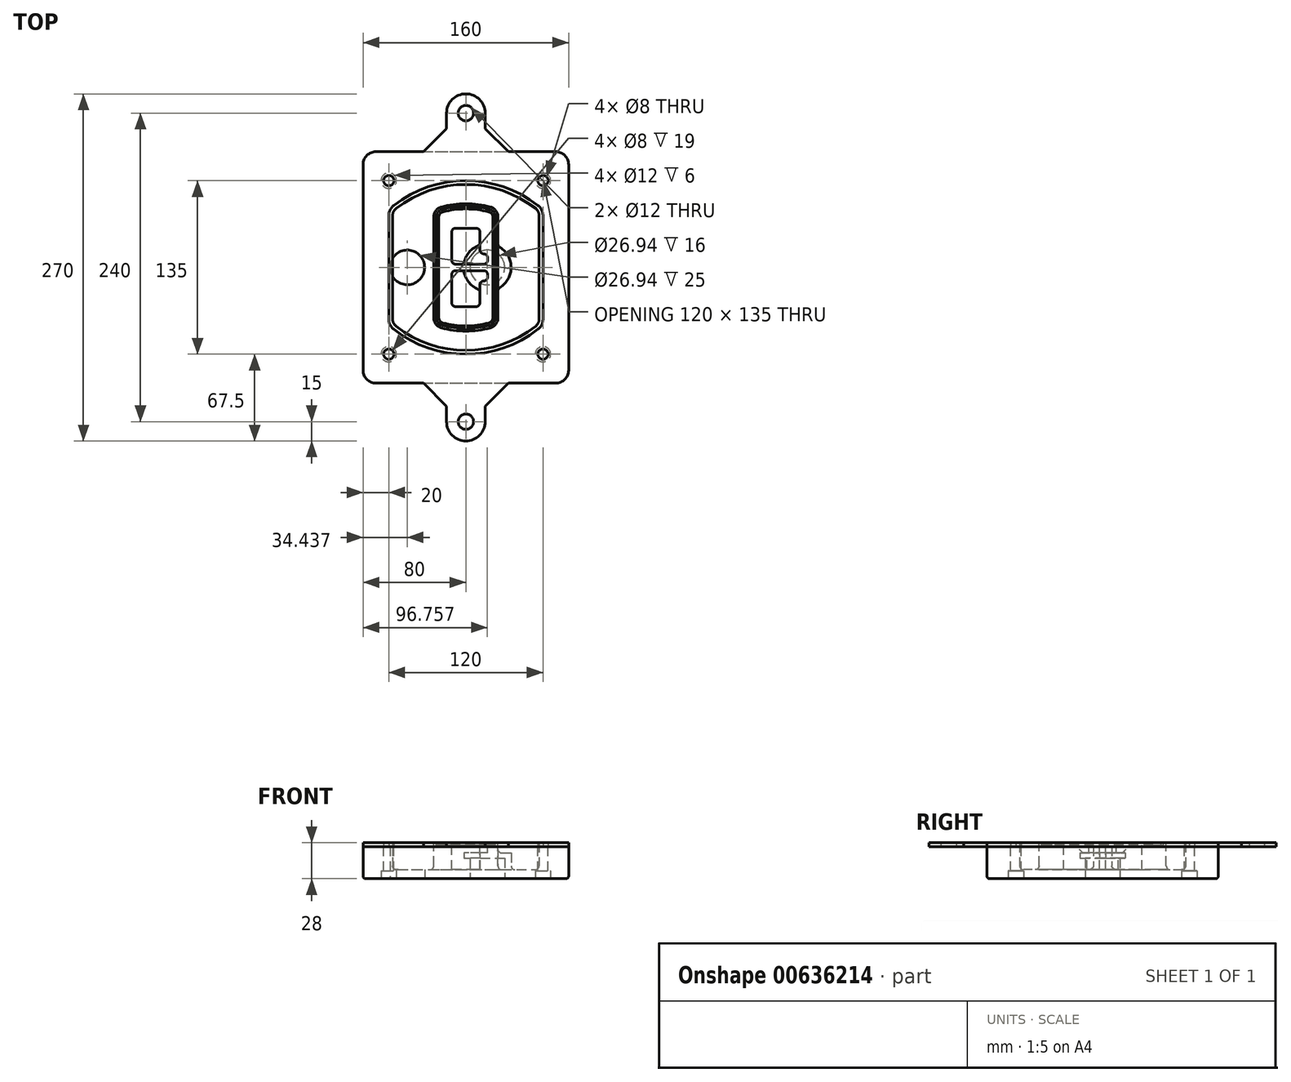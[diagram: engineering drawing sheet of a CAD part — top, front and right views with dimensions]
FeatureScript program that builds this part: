
annotation { "Feature Type Name" : "Feature", "Feature Type Description" : "" }
export const myFeature = defineFeature(function(context is Context, id is Id, definition is map)
    precondition{}
    {
        {
            var Q0;
            Q0=qCreatedBy(makeId("Top.planeOp"),FACE);
            var sketch = newSketch(context, id + "F0", { "sketchPlane" : qUnion([Q0])});
            skPoint(sketch, "E0.rect.middle", {"position": v(0, 0) * mm});
            skLineSegment(sketch, "E1.bottom", {"start": v(-70, -90) * mm, "end": v(70, -90) * mm});
            skLineSegment(sketch, "E1.top", {"start": v(-70, 90) * mm, "end": v(70, 90) * mm});
            skLineSegment(sketch, "E1.left", {"start": v(-80, -80) * mm, "end": v(-80, 80) * mm});
            skLineSegment(sketch, "E1.right", {"start": v(80, -80) * mm, "end": v(80, 80) * mm});
            skLineSegment(sketch, "E2", {"start": v(-80, 90) * mm, "end": v(80, -90) * mm, "construction": true});
            skLineSegment(sketch, "E3", {"start": v(80, 90) * mm, "end": v(-80, -90) * mm, "construction": true});
            skCircle(sketch, "E4", {"center": v(-60, 67.5) * mm, "radius": 4 * mm});
            skCircle(sketch, "E5", {"center": v(60, 67.5) * mm, "radius": 4 * mm});
            skCircle(sketch, "E6", {"center": v(60, -67.5) * mm, "radius": 4 * mm});
            skCircle(sketch, "E7", {"center": v(-60, -67.5) * mm, "radius": 4 * mm});
            skLineSegment(sketch, "E8", {"start": v(-60, 67.5) * mm, "end": v(60, 67.5) * mm, "construction": true});
            skLineSegment(sketch, "E9", {"start": v(60, 67.5) * mm, "end": v(60, -67.5) * mm, "construction": true});
            skLineSegment(sketch, "E10", {"start": v(60, -67.5) * mm, "end": v(-60, -67.5) * mm, "construction": true});
            skLineSegment(sketch, "E11", {"start": v(-60, -67.5) * mm, "end": v(-60, 67.5) * mm, "construction": true});
            skLineSegment(sketch, "E12", {"start": v(-60, 40.3) * mm, "end": v(-60, -40.3) * mm});
            skLineSegment(sketch, "E13", {"start": v(60, 40.3) * mm, "end": v(60, -40.3) * mm});
            skArc(sketch, "E14", {"start": v(56.15, 48.18) * mm, "mid": v(0, 67.5) * mm, "end": v(-56.15, 48.18) * mm});
            skArc(sketch, "E15", {"start": v(-56.15, -48.18) * mm, "mid": v(0, -67.5) * mm, "end": v(56.15, -48.18) * mm});
            skLineSegment(sketch, "E16", {"start": v(-60, 0) * mm, "end": v(60, 0) * mm, "construction": true});
            skPoint(sketch, "E17.visualSharp", {"position": v(-60, -45) * mm});
            skArc(sketch, "E17.filletArc", {"start": v(-60, -40.3) * mm, "mid": v(-58.99, -44.68) * mm, "end": v(-56.15, -48.18) * mm});
            skPoint(sketch, "E18.visualSharp", {"position": v(-60, 45) * mm});
            skArc(sketch, "E18.filletArc", {"start": v(-56.15, 48.18) * mm, "mid": v(-58.99, 44.68) * mm, "end": v(-60, 40.3) * mm});
            skPoint(sketch, "E19.visualSharp", {"position": v(60, 45) * mm});
            skArc(sketch, "E19.filletArc", {"start": v(60, 40.3) * mm, "mid": v(58.99, 44.68) * mm, "end": v(56.15, 48.18) * mm});
            skPoint(sketch, "E20.visualSharp", {"position": v(60, -45) * mm});
            skArc(sketch, "E20.filletArc", {"start": v(56.15, -48.18) * mm, "mid": v(58.99, -44.68) * mm, "end": v(60, -40.3) * mm});
            skPoint(sketch, "E21.visualSharp", {"position": v(-80, 90) * mm});
            skArc(sketch, "E21.filletArc", {"start": v(-70, 90) * mm, "mid": v(-77.07, 87.07) * mm, "end": v(-80, 80) * mm});
            skPoint(sketch, "E22.visualSharp", {"position": v(80, 90) * mm});
            skArc(sketch, "E22.filletArc", {"start": v(80, 80) * mm, "mid": v(77.07, 87.07) * mm, "end": v(70, 90) * mm});
            skPoint(sketch, "E23.visualSharp", {"position": v(80, -90) * mm});
            skArc(sketch, "E23.filletArc", {"start": v(70, -90) * mm, "mid": v(77.07, -87.07) * mm, "end": v(80, -80) * mm});
            skPoint(sketch, "E24.visualSharp", {"position": v(-80, -90) * mm});
            skArc(sketch, "E24.filletArc", {"start": v(-80, -80) * mm, "mid": v(-77.07, -87.07) * mm, "end": v(-70, -90) * mm});
            skArc(sketch, "E25.0", {"start": v(57, 40.3) * mm, "mid": v(56.3, 43.36) * mm, "end": v(54.3, 45.81) * mm});
            skLineSegment(sketch, "E25.1", {"start": v(57, 40.3) * mm, "end": v(57, -40.3) * mm});
            skArc(sketch, "E25.2", {"start": v(54.3, -45.81) * mm, "mid": v(56.3, -43.36) * mm, "end": v(57, -40.3) * mm});
            skArc(sketch, "E25.3", {"start": v(-54.3, -45.81) * mm, "mid": v(0, -64.5) * mm, "end": v(54.3, -45.81) * mm});
            skArc(sketch, "E25.4", {"start": v(-57, -40.3) * mm, "mid": v(-56.3, -43.36) * mm, "end": v(-54.3, -45.81) * mm});
            skArc(sketch, "E25.5", {"start": v(54.3, 45.81) * mm, "mid": v(0, 64.5) * mm, "end": v(-54.3, 45.81) * mm});
            skLineSegment(sketch, "E25.6", {"start": v(-57, 40.3) * mm, "end": v(-57, -40.3) * mm});
            skArc(sketch, "E25.7", {"start": v(-54.3, 45.81) * mm, "mid": v(-56.3, 43.36) * mm, "end": v(-57, 40.3) * mm});
            skArc(sketch, "E26.0", {"start": v(-58.62, 51.33) * mm, "mid": v(-62.58, 46.43) * mm, "end": v(-64, 40.3) * mm});
            skArc(sketch, "E26.1", {"start": v(58.62, 51.33) * mm, "mid": v(0, 71.5) * mm, "end": v(-58.62, 51.33) * mm});
            skArc(sketch, "E26.2", {"start": v(64, 40.3) * mm, "mid": v(62.58, 46.43) * mm, "end": v(58.62, 51.33) * mm});
            skLineSegment(sketch, "E26.3", {"start": v(64, 40.3) * mm, "end": v(64, -40.3) * mm});
            skArc(sketch, "E26.4", {"start": v(58.62, -51.33) * mm, "mid": v(62.58, -46.43) * mm, "end": v(64, -40.3) * mm});
            skLineSegment(sketch, "E26.5", {"start": v(-64, 40.3) * mm, "end": v(-64, -40.3) * mm});
            skArc(sketch, "E26.6", {"start": v(-58.62, -51.33) * mm, "mid": v(0, -71.5) * mm, "end": v(58.62, -51.33) * mm});
            skArc(sketch, "E26.7", {"start": v(-64, -40.3) * mm, "mid": v(-62.58, -46.43) * mm, "end": v(-58.62, -51.33) * mm});
            skSolve(sketch);
        }
        {
            var Q0;
            Q0=makeQuery(id+"F0.imprint","IMPRINT",FACE,{"disambiguationData":[TD([[makeQuery(id+"F0.imprint","IMPRINT",EDGE,{"derivedFrom":sQuery(id+"F0.wireOp",EDGE,"E1.bottom")}),1.0]])]});
            var Q1;
            Q1=makeQuery(id+"F0.imprint","IMPRINT",FACE,{"disambiguationData":[TD([[makeQuery(id+"F0.imprint","IMPRINT",EDGE,{"derivedFrom":sQuery(id+"F0.wireOp",EDGE,"E12")}),1.0]])]});
            var Q2;
            Q2=makeQuery(id+"F0.imprint","IMPRINT",FACE,{"disambiguationData":[TD([[makeQuery(id+"F0.imprint","IMPRINT",EDGE,{"derivedFrom":sQuery(id+"F0.wireOp",EDGE,"E25.0")}),1.0]])]});
            var Q3;
            Q3=makeQuery(id+"F0.imprint","IMPRINT",FACE,{"disambiguationData":[TD([[makeQuery(id+"F0.imprint","IMPRINT",EDGE,{"derivedFrom":sQuery(id+"F0.wireOp",EDGE,"E12")}),-1.0]])]});
            extrude(context, id + "F1", {"entities" : qUnion([Q0, Q1, Q2, Q3]), "oppositeDirection" : true, "depth" : 25 * mm});
        }
        {
            var Q0;
            Q0=makeQuery(id+"F0.imprint","IMPRINT",FACE,{"disambiguationData":[TD([[makeQuery(id+"F0.imprint","IMPRINT",EDGE,{"derivedFrom":sQuery(id+"F0.wireOp",EDGE,"E12")}),1.0]])]});
            extrude(context, id + "F2", {"entities" : qUnion([Q0]), "operationType" : NewBodyOperationType.ADD, "depth" : 3 * mm});
        }
        {
            var Q0;
            Q0=makeQuery(id+"F0.imprint","IMPRINT",FACE,{"disambiguationData":[TD([[makeQuery(id+"F0.imprint","IMPRINT",EDGE,{"derivedFrom":sQuery(id+"F0.wireOp",EDGE,"E25.0")}),1.0]])]});
            extrude(context, id + "F3", {"entities" : qUnion([Q0]), "operationType" : NewBodyOperationType.REMOVE, "oppositeDirection" : true, "depth" : 18 * mm});
        }
        {
            var Q0;
            Q0=makeQuery(id+"F2.opExtrude","CAP_FACE",FACE,{"disambiguationData":[OSD([sQuery(id+"F0.wireOp",EDGE,"E12"),sQuery(id+"F0.wireOp",EDGE,"E13"),sQuery(id+"F0.wireOp",EDGE,"E14"),sQuery(id+"F0.wireOp",EDGE,"E15"),sQuery(id+"F0.wireOp",EDGE,"E17.filletArc"),sQuery(id+"F0.wireOp",EDGE,"E18.filletArc"),sQuery(id+"F0.wireOp",EDGE,"E19.filletArc"),sQuery(id+"F0.wireOp",EDGE,"E20.filletArc"),sQuery(id+"F0.wireOp",EDGE,"E25.0"),sQuery(id+"F0.wireOp",EDGE,"E25.1"),sQuery(id+"F0.wireOp",EDGE,"E25.2"),sQuery(id+"F0.wireOp",EDGE,"E25.3"),sQuery(id+"F0.wireOp",EDGE,"E25.4"),sQuery(id+"F0.wireOp",EDGE,"E25.5"),sQuery(id+"F0.wireOp",EDGE,"E25.6"),sQuery(id+"F0.wireOp",EDGE,"E25.7")])],"isStart":false});
            var sketch = newSketch(context, id + "F4", { "sketchPlane" : qUnion([Q0])});
            skArc(sketch, "E27.0", {"start": v(-19.08, -46.97) * mm, "mid": v(0, -49.5) * mm, "end": v(19.08, -46.97) * mm});
            skArc(sketch, "E28.0", {"start": v(19.08, 46.97) * mm, "mid": v(0, 49.5) * mm, "end": v(-19.08, 46.97) * mm});
            skLineSegment(sketch, "E29", {"start": v(-25, 39.25) * mm, "end": v(-25, -39.25) * mm});
            skLineSegment(sketch, "E30", {"start": v(25, 39.25) * mm, "end": v(25, -39.25) * mm});
            skLineSegment(sketch, "E31", {"start": v(-25, 45.1) * mm, "end": v(25, 45.1) * mm, "construction": true});
            skLineSegment(sketch, "E32", {"start": v(-25, -45.1) * mm, "end": v(25, -45.1) * mm, "construction": true});
            skPoint(sketch, "E33.visualSharp", {"position": v(-25, 45.1) * mm});
            skArc(sketch, "E33.filletArc", {"start": v(-19.08, 46.97) * mm, "mid": v(-23.35, 44.11) * mm, "end": v(-25, 39.25) * mm});
            skPoint(sketch, "E34.visualSharp", {"position": v(25, 45.1) * mm});
            skArc(sketch, "E34.filletArc", {"start": v(25, 39.25) * mm, "mid": v(23.35, 44.11) * mm, "end": v(19.08, 46.97) * mm});
            skPoint(sketch, "E35.visualSharp", {"position": v(25, -45.1) * mm});
            skArc(sketch, "E35.filletArc", {"start": v(19.08, -46.97) * mm, "mid": v(23.35, -44.11) * mm, "end": v(25, -39.25) * mm});
            skPoint(sketch, "E36.visualSharp", {"position": v(-25, -45.1) * mm});
            skArc(sketch, "E36.filletArc", {"start": v(-25, -39.25) * mm, "mid": v(-23.35, -44.11) * mm, "end": v(-19.08, -46.97) * mm});
            skArc(sketch, "E37.0", {"start": v(54.3, 45.81) * mm, "mid": v(0, 64.5) * mm, "end": v(-54.3, 45.81) * mm});
            skArc(sketch, "E37.1", {"start": v(-54.3, 45.81) * mm, "mid": v(-56.3, 43.36) * mm, "end": v(-57, 40.3) * mm});
            skLineSegment(sketch, "E37.2", {"start": v(-57, 40.3) * mm, "end": v(-57, -40.3) * mm});
            skArc(sketch, "E37.3", {"start": v(-57, -40.3) * mm, "mid": v(-56.3, -43.36) * mm, "end": v(-54.3, -45.81) * mm});
            skArc(sketch, "E37.4", {"start": v(-54.3, -45.81) * mm, "mid": v(0, -64.5) * mm, "end": v(54.3, -45.81) * mm});
            skArc(sketch, "E37.5", {"start": v(54.3, -45.81) * mm, "mid": v(56.3, -43.36) * mm, "end": v(57, -40.3) * mm});
            skLineSegment(sketch, "E37.6", {"start": v(57, 40.3) * mm, "end": v(57, -40.3) * mm});
            skArc(sketch, "E37.7", {"start": v(57, 40.3) * mm, "mid": v(56.3, 43.36) * mm, "end": v(54.3, 45.81) * mm});
            skLineSegment(sketch, "E38.0", {"start": v(23, 39.25) * mm, "end": v(23, -39.25) * mm});
            skArc(sketch, "E38.1", {"start": v(18.56, -45.04) * mm, "mid": v(21.76, -42.9) * mm, "end": v(23, -39.25) * mm});
            skArc(sketch, "E38.2", {"start": v(-18.56, -45.04) * mm, "mid": v(0, -47.5) * mm, "end": v(18.56, -45.04) * mm});
            skArc(sketch, "E38.3", {"start": v(-23, -39.25) * mm, "mid": v(-21.76, -42.9) * mm, "end": v(-18.56, -45.04) * mm});
            skLineSegment(sketch, "E38.4", {"start": v(-23, 39.25) * mm, "end": v(-23, -39.25) * mm});
            skArc(sketch, "E38.5", {"start": v(23, 39.25) * mm, "mid": v(21.76, 42.9) * mm, "end": v(18.56, 45.04) * mm});
            skArc(sketch, "E38.6", {"start": v(-18.56, 45.04) * mm, "mid": v(-21.76, 42.9) * mm, "end": v(-23, 39.25) * mm});
            skArc(sketch, "E38.7", {"start": v(18.56, 45.04) * mm, "mid": v(0, 47.5) * mm, "end": v(-18.56, 45.04) * mm});
            skArc(sketch, "E39.0", {"start": v(21, 39.25) * mm, "mid": v(20.18, 41.68) * mm, "end": v(18.04, 43.1) * mm});
            skLineSegment(sketch, "E39.1", {"start": v(21, 39.25) * mm, "end": v(21, -39.25) * mm});
            skArc(sketch, "E39.2", {"start": v(18.04, -43.1) * mm, "mid": v(20.18, -41.68) * mm, "end": v(21, -39.25) * mm});
            skArc(sketch, "E39.3", {"start": v(-18.04, -43.1) * mm, "mid": v(0, -45.5) * mm, "end": v(18.04, -43.1) * mm});
            skArc(sketch, "E39.4", {"start": v(-21, -39.25) * mm, "mid": v(-20.18, -41.68) * mm, "end": v(-18.04, -43.1) * mm});
            skArc(sketch, "E39.5", {"start": v(18.04, 43.1) * mm, "mid": v(0, 45.5) * mm, "end": v(-18.04, 43.1) * mm});
            skLineSegment(sketch, "E39.6", {"start": v(-21, 39.25) * mm, "end": v(-21, -39.25) * mm});
            skArc(sketch, "E39.7", {"start": v(-18.04, 43.1) * mm, "mid": v(-20.18, 41.68) * mm, "end": v(-21, 39.25) * mm});
            skLineSegment(sketch, "E40", {"start": v(-25, 0) * mm, "end": v(25, 0) * mm, "construction": true});
            skLineSegment(sketch, "E41", {"start": v(-11, 5.5) * mm, "end": v(-11, 27.5) * mm});
            skLineSegment(sketch, "E42", {"start": v(-8, 30.5) * mm, "end": v(8, 30.5) * mm});
            skLineSegment(sketch, "E43", {"start": v(11, 27.5) * mm, "end": v(11, 13.5) * mm});
            skLineSegment(sketch, "E44", {"start": v(14, 10.5) * mm, "end": v(14, 10.5) * mm});
            skLineSegment(sketch, "E45", {"start": v(17, 7.5) * mm, "end": v(17, 5.5) * mm});
            skLineSegment(sketch, "E46", {"start": v(14, 2.5) * mm, "end": v(-8, 2.5) * mm});
            skPoint(sketch, "E47.visualSharp", {"position": v(-11, 30.5) * mm});
            skArc(sketch, "E47.filletArc", {"start": v(-8, 30.5) * mm, "mid": v(-10.12, 29.62) * mm, "end": v(-11, 27.5) * mm});
            skPoint(sketch, "E48.visualSharp", {"position": v(11, 30.5) * mm});
            skArc(sketch, "E48.filletArc", {"start": v(11, 27.5) * mm, "mid": v(10.12, 29.62) * mm, "end": v(8, 30.5) * mm});
            skPoint(sketch, "E49.visualSharp", {"position": v(11, 10.5) * mm});
            skArc(sketch, "E49.filletArc", {"start": v(11, 13.5) * mm, "mid": v(11.88, 11.38) * mm, "end": v(14, 10.5) * mm});
            skPoint(sketch, "E50.visualSharp", {"position": v(17, 10.5) * mm});
            skArc(sketch, "E50.filletArc", {"start": v(17, 7.5) * mm, "mid": v(16.12, 9.62) * mm, "end": v(14, 10.5) * mm});
            skPoint(sketch, "E51.visualSharp", {"position": v(17, 2.5) * mm});
            skArc(sketch, "E51.filletArc", {"start": v(14, 2.5) * mm, "mid": v(16.12, 3.38) * mm, "end": v(17, 5.5) * mm});
            skPoint(sketch, "E52.visualSharp", {"position": v(-11, 2.5) * mm});
            skArc(sketch, "E52.filletArc", {"start": v(-11, 5.5) * mm, "mid": v(-10.12, 3.38) * mm, "end": v(-8, 2.5) * mm});
            skLineSegment(sketch, "E53.0.MirrorCS", {"start": v(14, -2.5) * mm, "end": v(-8, -2.5) * mm});
            skArc(sketch, "E54.0.MirrorCS", {"start": v(-11, -5.5) * mm, "mid": v(-10.12, -3.38) * mm, "end": v(-8, -2.5) * mm});
            skLineSegment(sketch, "E55.0.MirrorCS", {"start": v(-11, -5.5) * mm, "end": v(-11, -27.5) * mm});
            skArc(sketch, "E56.0.MirrorCS", {"start": v(-8, -30.5) * mm, "mid": v(-10.12, -29.62) * mm, "end": v(-11, -27.5) * mm});
            skLineSegment(sketch, "E57.0.MirrorCS", {"start": v(-8, -30.5) * mm, "end": v(8, -30.5) * mm});
            skArc(sketch, "E58.0.MirrorCS", {"start": v(11, -27.5) * mm, "mid": v(10.12, -29.62) * mm, "end": v(8, -30.5) * mm});
            skLineSegment(sketch, "E59.0.MirrorCS", {"start": v(11, -27.5) * mm, "end": v(11, -13.5) * mm});
            skArc(sketch, "E60.0.MirrorCS", {"start": v(11, -13.5) * mm, "mid": v(11.88, -11.38) * mm, "end": v(14, -10.5) * mm});
            skArc(sketch, "E61.0.MirrorCS", {"start": v(17, -7.5) * mm, "mid": v(16.12, -9.62) * mm, "end": v(14, -10.5) * mm});
            skLineSegment(sketch, "E62.0.MirrorCS", {"start": v(17, -7.5) * mm, "end": v(17, -5.5) * mm});
            skArc(sketch, "E63.0.MirrorCS", {"start": v(14, -2.5) * mm, "mid": v(16.12, -3.38) * mm, "end": v(17, -5.5) * mm});
            skSolve(sketch);
        }
        {
            var Q0;
            Q0=makeQuery(id+"F4.imprint","IMPRINT",FACE,{"disambiguationData":[TD([[makeQuery(id+"F4.imprint","IMPRINT",EDGE,{"derivedFrom":sQuery(id+"F4.wireOp",EDGE,"E27.0")}),1.0]])]});
            var Q1;
            Q1=makeQuery(id+"F4.imprint","IMPRINT",FACE,{"disambiguationData":[TD([[makeQuery(id+"F4.imprint","IMPRINT",EDGE,{"derivedFrom":sQuery(id+"F4.wireOp",EDGE,"E38.0")}),-1.0]])]});
            var Q2;
            Q2=makeQuery(id+"F4.imprint","IMPRINT",FACE,{"disambiguationData":[TD([[makeQuery(id+"F4.imprint","IMPRINT",EDGE,{"derivedFrom":sQuery(id+"F4.wireOp",EDGE,"E39.0")}),1.0]])]});
            extrude(context, id + "F5", {"entities" : qUnion([Q0, Q1, Q2]), "operationType" : NewBodyOperationType.ADD, "endBound" : BoundingType.UP_TO_NEXT, "oppositeDirection" : true, "depth" : 25 * mm});
        }
        {
            var Q0;
            Q0=makeQuery(id+"F4.imprint","IMPRINT",FACE,{"disambiguationData":[TD([[makeQuery(id+"F4.imprint","IMPRINT",EDGE,{"derivedFrom":sQuery(id+"F4.wireOp",EDGE,"E38.0")}),-1.0]])]});
            extrude(context, id + "F6", {"entities" : qUnion([Q0]), "operationType" : NewBodyOperationType.REMOVE, "oppositeDirection" : true, "depth" : 2 * mm});
        }
        {
            var Q0;
            Q0=makeQuery(id+"F1.opExtrude","CAP_FACE",FACE,{"disambiguationData":[OSD([sQuery(id+"F0.wireOp",EDGE,"E1.bottom"),sQuery(id+"F0.wireOp",EDGE,"E1.top"),sQuery(id+"F0.wireOp",EDGE,"E1.left"),sQuery(id+"F0.wireOp",EDGE,"E1.right"),sQuery(id+"F0.wireOp",EDGE,"E4"),sQuery(id+"F0.wireOp",EDGE,"E5"),sQuery(id+"F0.wireOp",EDGE,"E6"),sQuery(id+"F0.wireOp",EDGE,"E7"),sQuery(id+"F0.wireOp",EDGE,"E21.filletArc"),sQuery(id+"F0.wireOp",EDGE,"E22.filletArc"),sQuery(id+"F0.wireOp",EDGE,"E23.filletArc"),sQuery(id+"F0.wireOp",EDGE,"E24.filletArc")])],"isStart":false});
            var sketch = newSketch(context, id + "F7", { "sketchPlane" : qUnion([Q0])});
            skCircle(sketch, "E64", {"center": v(16.76, 0) * mm, "radius": 13.47 * mm});
            skCircle(sketch, "E65", {"center": v(-45.56, 0) * mm, "radius": 13.47 * mm});
            skLineSegment(sketch, "E66", {"start": v(80, 0) * mm, "end": v(-80, 0) * mm});
            skCircle(sketch, "E67", {"center": v(16.76, 0) * mm, "radius": 18.47 * mm});
            skCircle(sketch, "E68", {"center": v(60, -67.5) * mm, "radius": 6 * mm});
            skCircle(sketch, "E69", {"center": v(-60, -67.5) * mm, "radius": 6 * mm});
            skCircle(sketch, "E70", {"center": v(-60, 67.5) * mm, "radius": 6 * mm});
            skCircle(sketch, "E71", {"center": v(60, 67.5) * mm, "radius": 6 * mm});
            skSolve(sketch);
        }
        {
            var Q0;
            {var subQ1=sQuery(id+"F7.wireOp",EDGE,"E66");var subQ4=sQuery(id+"F7.wireOp",EDGE,"E64");var subQ6=makeQuery(id+"F7.imprint","INTERSECT",VERTEX,{"disambiguationData":[OD(0.0)],"derivedFrom":[subQ4,subQ1]});Q0=makeQuery(id+"F7.imprint","IMPRINT",FACE,{"disambiguationData":[TD([[makeQuery(id+"F7.imprint","IMPRINT",EDGE,{"disambiguationData":[TD([[subQ6,-1.0]])],"derivedFrom":subQ4}),-1.0]])]});}
            var Q1;
            {var subQ0=sQuery(id+"F7.wireOp",EDGE,"E66");var subQ1=sQuery(id+"F7.wireOp",EDGE,"E64");var subQ3=makeQuery(id+"F7.imprint","INTERSECT",VERTEX,{"disambiguationData":[OD(0.0)],"derivedFrom":[subQ1,subQ0]});Q1=makeQuery(id+"F7.imprint","IMPRINT",FACE,{"disambiguationData":[TD([[makeQuery(id+"F7.imprint","IMPRINT",EDGE,{"disambiguationData":[TD([[subQ3,-1.0]])],"derivedFrom":subQ1}),1.0]])]});}
            var Q2;
            {var subQ0=sQuery(id+"F7.wireOp",EDGE,"E66");var subQ1=sQuery(id+"F7.wireOp",EDGE,"E64");var subQ3=makeQuery(id+"F7.imprint","INTERSECT",VERTEX,{"disambiguationData":[OD(0.0)],"derivedFrom":[subQ1,subQ0]});Q2=makeQuery(id+"F7.imprint","IMPRINT",FACE,{"disambiguationData":[TD([[makeQuery(id+"F7.imprint","IMPRINT",EDGE,{"disambiguationData":[TD([[subQ3,1.0]])],"derivedFrom":subQ1}),1.0]])]});}
            var Q3;
            {var subQ1=sQuery(id+"F7.wireOp",EDGE,"E66");var subQ4=sQuery(id+"F7.wireOp",EDGE,"E64");var subQ6=makeQuery(id+"F7.imprint","INTERSECT",VERTEX,{"disambiguationData":[OD(0.0)],"derivedFrom":[subQ4,subQ1]});Q3=makeQuery(id+"F7.imprint","IMPRINT",FACE,{"disambiguationData":[TD([[makeQuery(id+"F7.imprint","IMPRINT",EDGE,{"disambiguationData":[TD([[subQ6,1.0]])],"derivedFrom":subQ4}),-1.0]])]});}
            extrude(context, id + "F8", {"entities" : qUnion([Q0, Q1, Q2, Q3]), "operationType" : NewBodyOperationType.ADD, "oppositeDirection" : true, "depth" : 20 * mm});
        }
        {
            var Q0;
            {var subQ0=sQuery(id+"F7.wireOp",EDGE,"E66");var subQ1=sQuery(id+"F7.wireOp",EDGE,"E64");var subQ3=makeQuery(id+"F7.imprint","INTERSECT",VERTEX,{"disambiguationData":[OD(0.0)],"derivedFrom":[subQ1,subQ0]});Q0=makeQuery(id+"F7.imprint","IMPRINT",FACE,{"disambiguationData":[TD([[makeQuery(id+"F7.imprint","IMPRINT",EDGE,{"disambiguationData":[TD([[subQ3,-1.0]])],"derivedFrom":subQ1}),1.0]])]});}
            var Q1;
            {var subQ0=sQuery(id+"F7.wireOp",EDGE,"E66");var subQ1=sQuery(id+"F7.wireOp",EDGE,"E64");var subQ3=makeQuery(id+"F7.imprint","INTERSECT",VERTEX,{"disambiguationData":[OD(0.0)],"derivedFrom":[subQ1,subQ0]});Q1=makeQuery(id+"F7.imprint","IMPRINT",FACE,{"disambiguationData":[TD([[makeQuery(id+"F7.imprint","IMPRINT",EDGE,{"disambiguationData":[TD([[subQ3,1.0]])],"derivedFrom":subQ1}),1.0]])]});}
            extrude(context, id + "F9", {"entities" : qUnion([Q0, Q1]), "operationType" : NewBodyOperationType.REMOVE, "oppositeDirection" : true, "depth" : 16 * mm});
        }
        {
            var Q0;
            {var subQ0=sQuery(id+"F7.wireOp",EDGE,"E66");var subQ1=sQuery(id+"F7.wireOp",EDGE,"E65");var subQ3=makeQuery(id+"F7.imprint","INTERSECT",VERTEX,{"disambiguationData":[OD(0.0)],"derivedFrom":[subQ1,subQ0]});Q0=makeQuery(id+"F7.imprint","IMPRINT",FACE,{"disambiguationData":[TD([[makeQuery(id+"F7.imprint","IMPRINT",EDGE,{"disambiguationData":[TD([[subQ3,-1.0]])],"derivedFrom":subQ1}),1.0]])]});}
            var Q1;
            {var subQ0=sQuery(id+"F7.wireOp",EDGE,"E66");var subQ1=sQuery(id+"F7.wireOp",EDGE,"E65");var subQ3=makeQuery(id+"F7.imprint","INTERSECT",VERTEX,{"disambiguationData":[OD(0.0)],"derivedFrom":[subQ1,subQ0]});Q1=makeQuery(id+"F7.imprint","IMPRINT",FACE,{"disambiguationData":[TD([[makeQuery(id+"F7.imprint","IMPRINT",EDGE,{"disambiguationData":[TD([[subQ3,1.0]])],"derivedFrom":subQ1}),1.0]])]});}
            extrude(context, id + "F10", {"entities" : qUnion([Q0, Q1]), "operationType" : NewBodyOperationType.REMOVE, "oppositeDirection" : true, "depth" : 25 * mm});
        }
        {
            var Q0;
            Q0=makeQuery(id+"F7.imprint","IMPRINT",FACE,{"disambiguationData":[TD([[makeQuery(id+"F7.imprint","IMPRINT",EDGE,{"derivedFrom":sQuery(id+"F7.wireOp",EDGE,"E68")}),1.0]])]});
            var Q1;
            Q1=makeQuery(id+"F7.imprint","IMPRINT",FACE,{"disambiguationData":[TD([[makeQuery(id+"F7.imprint","IMPRINT",EDGE,{"derivedFrom":makeQuery(id+"F1.opExtrude","CAP_EDGE",EDGE,{"disambiguationData":[OSD([sQuery(id+"F0.wireOp",EDGE,"E5")])],"isStart":false})}),-1.0]])]});
            var Q2;
            Q2=makeQuery(id+"F7.imprint","IMPRINT",FACE,{"disambiguationData":[TD([[makeQuery(id+"F7.imprint","IMPRINT",EDGE,{"derivedFrom":sQuery(id+"F7.wireOp",EDGE,"E69")}),1.0]])]});
            var Q3;
            Q3=makeQuery(id+"F7.imprint","IMPRINT",FACE,{"disambiguationData":[TD([[makeQuery(id+"F7.imprint","IMPRINT",EDGE,{"derivedFrom":makeQuery(id+"F1.opExtrude","CAP_EDGE",EDGE,{"disambiguationData":[OSD([sQuery(id+"F0.wireOp",EDGE,"E4")])],"isStart":false})}),-1.0]])]});
            var Q4;
            Q4=makeQuery(id+"F7.imprint","IMPRINT",FACE,{"disambiguationData":[TD([[makeQuery(id+"F7.imprint","IMPRINT",EDGE,{"derivedFrom":sQuery(id+"F7.wireOp",EDGE,"E70")}),1.0]])]});
            var Q5;
            Q5=makeQuery(id+"F7.imprint","IMPRINT",FACE,{"disambiguationData":[TD([[makeQuery(id+"F7.imprint","IMPRINT",EDGE,{"derivedFrom":makeQuery(id+"F1.opExtrude","CAP_EDGE",EDGE,{"disambiguationData":[OSD([sQuery(id+"F0.wireOp",EDGE,"E7")])],"isStart":false})}),-1.0]])]});
            var Q6;
            Q6=makeQuery(id+"F7.imprint","IMPRINT",FACE,{"disambiguationData":[TD([[makeQuery(id+"F7.imprint","IMPRINT",EDGE,{"derivedFrom":sQuery(id+"F7.wireOp",EDGE,"E71")}),1.0]])]});
            var Q7;
            Q7=makeQuery(id+"F7.imprint","IMPRINT",FACE,{"disambiguationData":[TD([[makeQuery(id+"F7.imprint","IMPRINT",EDGE,{"derivedFrom":makeQuery(id+"F1.opExtrude","CAP_EDGE",EDGE,{"disambiguationData":[OSD([sQuery(id+"F0.wireOp",EDGE,"E6")])],"isStart":false})}),-1.0]])]});
            extrude(context, id + "F11", {"entities" : qUnion([Q0, Q1, Q2, Q3, Q4, Q5, Q6, Q7]), "operationType" : NewBodyOperationType.REMOVE, "oppositeDirection" : true, "depth" : 6 * mm});
        }
        {
            var Q0;
            Q0=makeQuery(id+"F9.boolean.opBoolean","COPY",FACE,{"derivedFrom":makeQuery(id+"F9.opExtrude","CAP_FACE",FACE,{"disambiguationData":[OSD([sQuery(id+"F7.wireOp",EDGE,"E64")])],"isStart":false})});
            var sketch = newSketch(context, id + "F12", { "sketchPlane" : qUnion([Q0])});
            skArc(sketch, "E72.0", {"start": v(11, 17.55) * mm, "mid": v(2.57, 11.82) * mm, "end": v(-1.54, 2.5) * mm});
            skArc(sketch, "E72.1", {"start": v(-1.54, -2.5) * mm, "mid": v(2.57, -11.82) * mm, "end": v(11, -17.55) * mm});
            skLineSegment(sketch, "E73", {"start": v(-1.54, -2.5) * mm, "end": v(14, -2.5) * mm});
            skLineSegment(sketch, "E74.0", {"start": v(14, 2.5) * mm, "end": v(-1.54, 2.5) * mm});
            skArc(sketch, "E74.1", {"start": v(14, 2.5) * mm, "mid": v(16.12, 3.38) * mm, "end": v(17, 5.5) * mm});
            skLineSegment(sketch, "E74.2", {"start": v(17, 7.5) * mm, "end": v(17, 5.5) * mm});
            skArc(sketch, "E74.3", {"start": v(17, 7.5) * mm, "mid": v(16.12, 9.62) * mm, "end": v(14, 10.5) * mm});
            skArc(sketch, "E74.4", {"start": v(11, 13.5) * mm, "mid": v(11.88, 11.38) * mm, "end": v(14, 10.5) * mm});
            skLineSegment(sketch, "E74.5", {"start": v(11, 17.55) * mm, "end": v(11, 13.5) * mm});
            skLineSegment(sketch, "E74.7", {"start": v(14, -2.5) * mm, "end": v(-1.54, -2.5) * mm});
            skArc(sketch, "E74.8", {"start": v(14, -2.5) * mm, "mid": v(16.12, -3.38) * mm, "end": v(17, -5.5) * mm});
            skLineSegment(sketch, "E74.9", {"start": v(17, -7.5) * mm, "end": v(17, -5.5) * mm});
            skArc(sketch, "E74.10", {"start": v(17, -7.5) * mm, "mid": v(16.12, -9.62) * mm, "end": v(14, -10.5) * mm});
            skArc(sketch, "E74.11", {"start": v(11, -13.5) * mm, "mid": v(11.88, -11.38) * mm, "end": v(14, -10.5) * mm});
            skLineSegment(sketch, "E74.12", {"start": v(11, -17.55) * mm, "end": v(11, -13.5) * mm});
            skPoint(sketch, "E75.orphan", {"position": v(11, -27.5) * mm});
            skPoint(sketch, "E76.orphan", {"position": v(-8, -2.5) * mm});
            skPoint(sketch, "E77.orphan", {"position": v(-8, 2.5) * mm});
            skPoint(sketch, "E78.orphan", {"position": v(11, 27.5) * mm});
            skSolve(sketch);
        }
        {
            var Q0;
            {var subQ7=sQuery(id+"F12.wireOp",EDGE,"E72.0");var subQ14=sQuery(id+"F12.wireOp",EDGE,"E72.1");var subQ16=sQuery(id+"F12.wireOp",EDGE,"E74.1");var subQ18=sQuery(id+"F12.wireOp",EDGE,"E74.8");Q0=qUnion([makeQuery(id+"F12.imprint","IMPRINT",FACE,{"disambiguationData":[TD([[makeQuery(id+"F12.imprint","IMPRINT",EDGE,{"derivedFrom":subQ7}),1.0]])]}),makeQuery(id+"F12.imprint","IMPRINT",FACE,{"disambiguationData":[TD([[makeQuery(id+"F12.imprint","IMPRINT",EDGE,{"derivedFrom":subQ14}),1.0]])]}),makeQuery(id+"F12.imprint","IMPRINT",FACE,{"disambiguationData":[TD([[makeQuery(id+"F12.imprint","IMPRINT",EDGE,{"derivedFrom":subQ16}),1.0]])]}),makeQuery(id+"F12.imprint","IMPRINT",FACE,{"disambiguationData":[TD([[makeQuery(id+"F12.imprint","IMPRINT",EDGE,{"derivedFrom":subQ18}),-1.0]])]})]);}
            var Q1;
            Q1=makeQuery(id+"F5.boolean.opBoolean","SPLIT",FACE,{"disambiguationData":[TD([makeQuery(id+"F5.opExtrude","SWEPT_FACE",FACE,{"disambiguationData":[OSD([sQuery(id+"F4.wireOp",EDGE,"E41")])]})])],"derivedFrom":makeQuery(id+"F3.boolean.opBoolean","COPY",FACE,{"derivedFrom":makeQuery(id+"F3.opExtrude","CAP_FACE",FACE,{"disambiguationData":[OSD([sQuery(id+"F0.wireOp",EDGE,"E25.0"),sQuery(id+"F0.wireOp",EDGE,"E25.1"),sQuery(id+"F0.wireOp",EDGE,"E25.2"),sQuery(id+"F0.wireOp",EDGE,"E25.3"),sQuery(id+"F0.wireOp",EDGE,"E25.4"),sQuery(id+"F0.wireOp",EDGE,"E25.5"),sQuery(id+"F0.wireOp",EDGE,"E25.6"),sQuery(id+"F0.wireOp",EDGE,"E25.7")])],"isStart":false})})});
            extrude(context, id + "F13", {"entities" : qUnion([Q0]), "operationType" : NewBodyOperationType.REMOVE, "endBound" : BoundingType.UP_TO_SURFACE, "endBoundEntityFace" : qUnion([Q1]), "depth" : 25 * mm});
        }
        {
            var Q0;
            Q0=makeQuery(id+"F3.boolean.opBoolean","COPY",EDGE,{"derivedFrom":makeQuery(id+"F3.opExtrude","CAP_EDGE",EDGE,{"disambiguationData":[OSD([sQuery(id+"F0.wireOp",EDGE,"E25.6")])],"isStart":false})});
            var Q1;
            Q1=makeQuery(id+"F8.boolean.opBoolean","INTERSECT",EDGE,{"derivedFrom":[makeQuery(id+"F5.opExtrude","SWEPT_FACE",FACE,{"disambiguationData":[OSD([sQuery(id+"F4.wireOp",EDGE,"E30")])]}),makeQuery(id+"F8.opExtrude","CAP_FACE",FACE,{"disambiguationData":[OSD([sQuery(id+"F7.wireOp",EDGE,"E67")])],"isStart":false})]});
            var Q2;
            Q2=makeQuery(id+"F8.boolean.opBoolean","INTERSECT",EDGE,{"disambiguationData":[OD(1.0)],"derivedFrom":[makeQuery(id+"F5.opExtrude","SWEPT_FACE",FACE,{"disambiguationData":[OSD([sQuery(id+"F4.wireOp",EDGE,"E30")])]}),makeQuery(id+"F8.opExtrude","SWEPT_FACE",FACE,{"disambiguationData":[OSD([sQuery(id+"F7.wireOp",EDGE,"E67")])]})]});
            var Q3;
            {var subQ0=sQuery(id+"F4.wireOp",EDGE,"E30");Q3=makeQuery(id+"F8.boolean.opBoolean","SPLIT",EDGE,{"disambiguationData":[TD([makeQuery(id+"F5.opExtrude","SWEPT_FACE",FACE,{"disambiguationData":[OSD([sQuery(id+"F4.wireOp",EDGE,"E35.filletArc")])]})])],"derivedFrom":makeQuery(id+"F5.opExtrude","CAP_EDGE",EDGE,{"disambiguationData":[OSD([subQ0])],"isStart":false})});}
            var Q4;
            {var subQ0=sQuery(id+"F0.wireOp",EDGE,"E25.7");var subQ1=sQuery(id+"F0.wireOp",EDGE,"E25.1");var subQ2=sQuery(id+"F0.wireOp",EDGE,"E25.6");var subQ3=sQuery(id+"F0.wireOp",EDGE,"E25.5");var subQ4=sQuery(id+"F0.wireOp",EDGE,"E25.4");var subQ5=sQuery(id+"F0.wireOp",EDGE,"E25.0");var subQ6=sQuery(id+"F0.wireOp",EDGE,"E25.2");var subQ7=sQuery(id+"F0.wireOp",EDGE,"E25.3");Q4=makeQuery(id+"F8.boolean.opBoolean","INTERSECT",EDGE,{"derivedFrom":[makeQuery(id+"F5.boolean.opBoolean","SPLIT",FACE,{"disambiguationData":[TD([makeQuery(id+"F2.opExtrude","SWEPT_FACE",FACE,{"disambiguationData":[OSD([subQ5])]})])],"derivedFrom":makeQuery(id+"F3.boolean.opBoolean","COPY",FACE,{"derivedFrom":makeQuery(id+"F3.opExtrude","CAP_FACE",FACE,{"disambiguationData":[OSD([subQ5,subQ1,subQ6,subQ7,subQ4,subQ3,subQ2,subQ0])],"isStart":false})})}),makeQuery(id+"F8.opExtrude","SWEPT_FACE",FACE,{"disambiguationData":[OSD([sQuery(id+"F7.wireOp",EDGE,"E67")])]})]});}
            var Q5;
            Q5=makeQuery(id+"F8.boolean.opBoolean","INTERSECT",EDGE,{"disambiguationData":[OD(0.0)],"derivedFrom":[makeQuery(id+"F5.opExtrude","SWEPT_FACE",FACE,{"disambiguationData":[OSD([sQuery(id+"F4.wireOp",EDGE,"E30")])]}),makeQuery(id+"F8.opExtrude","SWEPT_FACE",FACE,{"disambiguationData":[OSD([sQuery(id+"F7.wireOp",EDGE,"E67")])]})]});
            fillet(context, id + "F14", {"entities" : qUnion([Q0, Q1, Q2, Q3, Q4, Q5]), "radius" : 3 * mm, "tangentPropagation" : true, "allowEdgeOverflow" : false});
        }
        {
            var Q0;
            Q0=makeQuery(id+"F1.opExtrude","CAP_EDGE",EDGE,{"disambiguationData":[OSD([sQuery(id+"F0.wireOp",EDGE,"E1.bottom")])],"isStart":false});
            fillet(context, id + "F15", {"entities" : qUnion([Q0]), "radius" : 2 * mm, "tangentPropagation" : true, "allowEdgeOverflow" : false});
        }
        {
            var Q0;
            {var subQ0=sQuery(id+"F0.wireOp",EDGE,"E21.filletArc");var subQ1=sQuery(id+"F0.wireOp",EDGE,"E7");var subQ2=sQuery(id+"F0.wireOp",EDGE,"E6");var subQ3=sQuery(id+"F0.wireOp",EDGE,"E5");var subQ4=sQuery(id+"F0.wireOp",EDGE,"E4");var subQ5=sQuery(id+"F0.wireOp",EDGE,"E22.filletArc");var subQ6=sQuery(id+"F0.wireOp",EDGE,"E1.bottom");var subQ7=sQuery(id+"F0.wireOp",EDGE,"E1.right");var subQ8=sQuery(id+"F0.wireOp",EDGE,"E1.top");var subQ9=sQuery(id+"F0.wireOp",EDGE,"E1.left");var subQ10=sQuery(id+"F0.wireOp",EDGE,"E23.filletArc");var subQ11=sQuery(id+"F0.wireOp",EDGE,"E24.filletArc");Q0=makeQuery(id+"F2.boolean.opBoolean","SPLIT",FACE,{"disambiguationData":[TD([makeQuery(id+"F1.opExtrude","SWEPT_FACE",FACE,{"disambiguationData":[OSD([subQ6])]})])],"derivedFrom":makeQuery(id+"F1.opExtrude","CAP_FACE",FACE,{"disambiguationData":[OSD([subQ6,subQ8,subQ9,subQ7,subQ4,subQ3,subQ2,subQ1,subQ0,subQ5,subQ10,subQ11])],"isStart":true})});}
            var sketch = newSketch(context, id + "F16", { "sketchPlane" : qUnion([Q0])});
            skLineSegment(sketch, "E79", {"start": v(0, 90) * mm, "end": v(0, 120) * mm, "construction": true});
            skArc(sketch, "E80", {"start": v(15, 120) * mm, "mid": v(0, 135) * mm, "end": v(-15, 120) * mm});
            skCircle(sketch, "E81", {"center": v(0, 120) * mm, "radius": 6 * mm});
            skLineSegment(sketch, "E82", {"start": v(-15, 120) * mm, "end": v(-15, 108) * mm});
            skLineSegment(sketch, "E83", {"start": v(15, 120) * mm, "end": v(15, 108) * mm});
            skLineSegment(sketch, "E84", {"start": v(15, 108) * mm, "end": v(33, 90) * mm});
            skLineSegment(sketch, "E85", {"start": v(-15, 108) * mm, "end": v(-33, 90) * mm});
            skLineSegment(sketch, "E86", {"start": v(-80, 0) * mm, "end": v(80, 0) * mm, "construction": true});
            skArc(sketch, "E87.MirrorCS", {"start": v(15, -120) * mm, "mid": v(0, -135) * mm, "end": v(-15, -120) * mm});
            skLineSegment(sketch, "E88.MirrorCS", {"start": v(-15, -108) * mm, "end": v(-33, -90) * mm});
            skLineSegment(sketch, "E89.MirrorCS", {"start": v(15, -108) * mm, "end": v(33, -90) * mm});
            skLineSegment(sketch, "E90.MirrorCS", {"start": v(15, -120) * mm, "end": v(15, -108) * mm});
            skLineSegment(sketch, "E91.MirrorCS", {"start": v(-15, -120) * mm, "end": v(-15, -108) * mm});
            skCircle(sketch, "E92.MirrorC", {"center": v(0, -120) * mm, "radius": 6 * mm});
            skLineSegment(sketch, "E93.MirrorCS", {"start": v(0, -90) * mm, "end": v(0, -120) * mm, "construction": true});
            skSolve(sketch);
        }
        {
            var Q0;
            {var subQ1=sQuery(id+"F16.wireOp",EDGE,"E88.MirrorCS");Q0=makeQuery(id+"F16.imprint","IMPRINT",FACE,{"disambiguationData":[TD([[makeQuery(id+"F16.imprint","IMPRINT",EDGE,{"derivedFrom":subQ1}),-1.0]])]});}
            var Q1;
            Q1=makeQuery(id+"F16.imprint","IMPRINT",FACE,{"disambiguationData":[TD([[makeQuery(id+"F16.imprint","IMPRINT",EDGE,{"derivedFrom":makeQuery(id+"F1.opExtrude","CAP_EDGE",EDGE,{"disambiguationData":[OSD([sQuery(id+"F0.wireOp",EDGE,"E1.left")])],"isStart":true})}),-1.0]])]});
            var Q2;
            Q2=makeQuery(id+"F16.imprint","IMPRINT",FACE,{"disambiguationData":[TD([[makeQuery(id+"F16.imprint","IMPRINT",EDGE,{"derivedFrom":sQuery(id+"F16.wireOp",EDGE,"E80")}),1.0]])]});
            var Q3;
            Q3=makeQuery(id+"F2.opExtrude","CAP_FACE",FACE,{"disambiguationData":[OSD([sQuery(id+"F0.wireOp",EDGE,"E12"),sQuery(id+"F0.wireOp",EDGE,"E13"),sQuery(id+"F0.wireOp",EDGE,"E14"),sQuery(id+"F0.wireOp",EDGE,"E15"),sQuery(id+"F0.wireOp",EDGE,"E17.filletArc"),sQuery(id+"F0.wireOp",EDGE,"E18.filletArc"),sQuery(id+"F0.wireOp",EDGE,"E19.filletArc"),sQuery(id+"F0.wireOp",EDGE,"E20.filletArc"),sQuery(id+"F0.wireOp",EDGE,"E25.0"),sQuery(id+"F0.wireOp",EDGE,"E25.1"),sQuery(id+"F0.wireOp",EDGE,"E25.2"),sQuery(id+"F0.wireOp",EDGE,"E25.3"),sQuery(id+"F0.wireOp",EDGE,"E25.4"),sQuery(id+"F0.wireOp",EDGE,"E25.5"),sQuery(id+"F0.wireOp",EDGE,"E25.6"),sQuery(id+"F0.wireOp",EDGE,"E25.7")])],"isStart":false});
            extrude(context, id + "F17", {"entities" : qUnion([Q0, Q1, Q2]), "endBound" : BoundingType.UP_TO_SURFACE, "depth" : 25 * mm, "endBoundEntityFace" : qUnion([Q3]), "offsetDistance" : 25 * mm});
        }
    });
